# Revit family: Haworth_Riverbend_StraightBench_EU_PRELIMINARY
name_source: partatom
category: Furniture
revit_build: Autodesk Revit 2018 (Build: 20170223_1515(x64)
units: mm (PartAtom-declared; Revit-internal decimal feet)

## family parameters
Always vertical = Yes
Cut with Voids When Loaded = No
OmniClass Number = 23.40.70.14.64.21
OmniClass Title = Systems Furniture
Room Calculation Point = No
Shared = No
Work Plane-Based = No

## types (8) — shared parameters
79D = No
85D = Yes
Actual Depth = 85 cm
Actual Height = 45 cm
Arms = Not available for No Back
Assembly Code = E2020200
Description = Haworth - Riverbend - Straight Bench
Front Finish = Haworth _ Plastic _ Black
Hardware Finish = Haworth _ Paint _ Plaster
Manufacturer = Haworth
Model = SELSSLNX
Revision Number = 1
Size = Verify Final Dim. w/ Haworth
Trim Finish = Haworth _ Paint _ Plaster
URL = https://www.haworth.com
URL - Product = https://www.haworth.com
Warranty = http://www.haworth.com

## per-type parameters (varying)
| type | Actual Width | High Back | Large | Medium | Mid Back | No Back | Small |
| 45 x 85 x 70 - No Back | 70 cm | No | No | No | No | Yes | Yes |
| 45 x 85 x 140 - No Back | 140 cm | No | No | Yes | No | Yes | No |
| 45 x 85 x 170 - No Back | 170 cm | No | Yes | No | No | Yes | No |
| 78 x 85 x 70 - Mid Back | 70 cm | No | No | No | Yes | No | Yes |
| 78 x 85 x 140 - Mid Back | 140 cm | No | No | Yes | Yes | No | No |
| 78 x 85 x 170 - Mid Back | 170 cm | No | Yes | No | Yes | No | No |
| 126 x 85 x 140 - High Back | 140 cm | Yes | No | Yes | No | No | No |
| 126 x 85 x 170 - High Back | 170 cm | Yes | Yes | No | No | No | No |

## geometry (parser evidence)
native form markers: Sweep x23
no freeform markers — native parametric forms only
